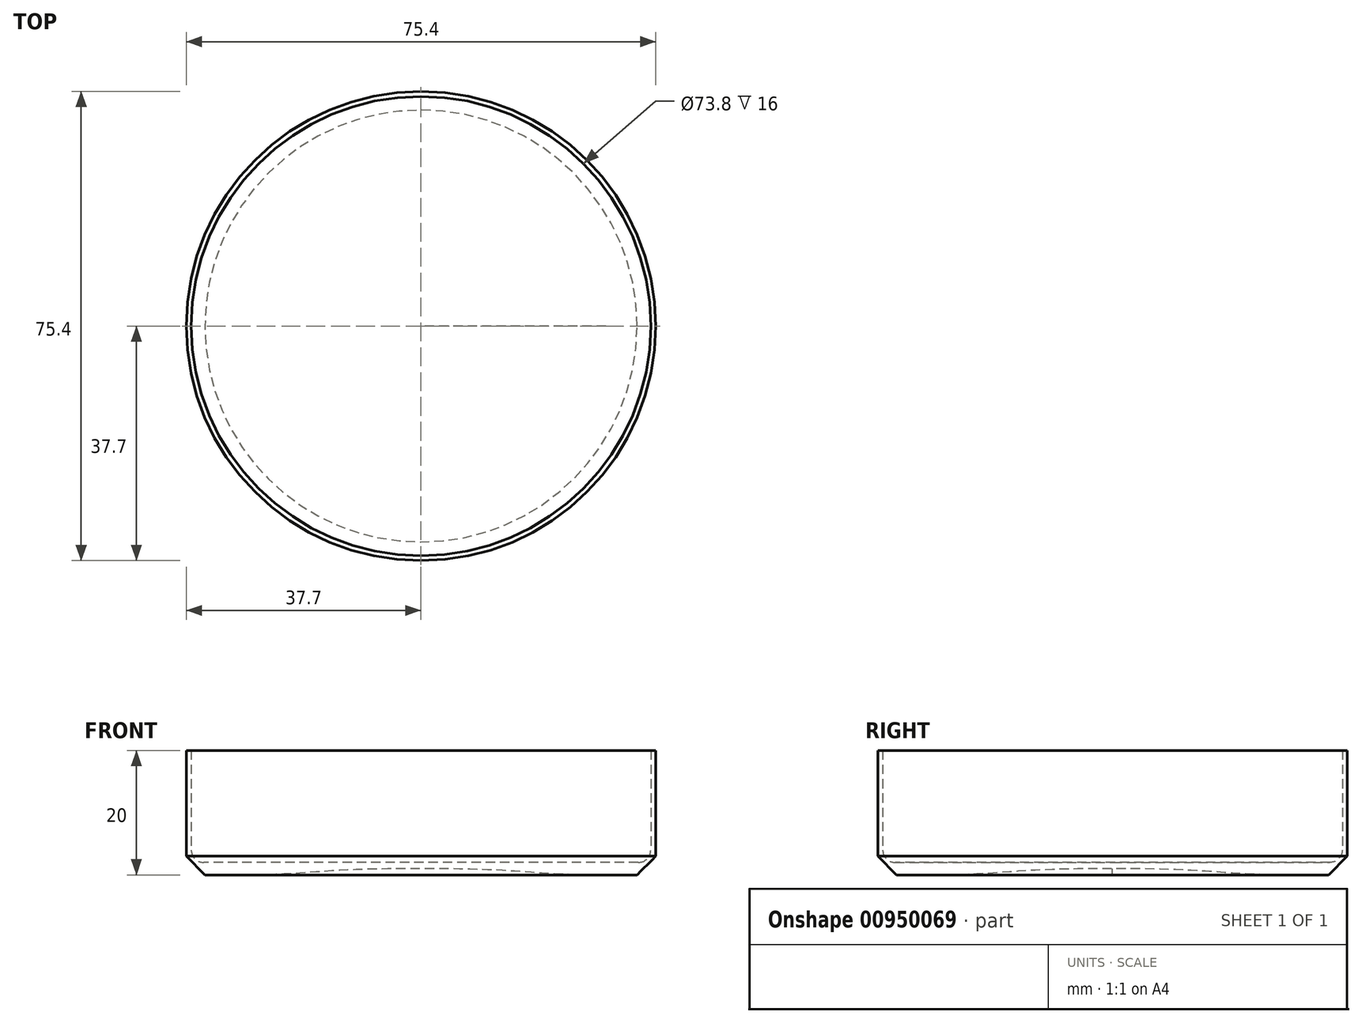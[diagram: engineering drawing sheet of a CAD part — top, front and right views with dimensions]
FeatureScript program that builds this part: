
annotation { "Feature Type Name" : "Feature", "Feature Type Description" : "" }
export const myFeature = defineFeature(function(context is Context, id is Id, definition is map)
    precondition{}
    {
        {
            var Q0;
            Q0=qCreatedBy(makeId("Front.planeOp"),FACE);
            var sketch = newSketch(context, id + "F0", { "sketchPlane" : qUnion([Q0])});
            skLineSegment(sketch, "E0", {"start": v(0, 0) * mm, "end": v(0, 38.46) * mm, "construction": true});
            skLineSegment(sketch, "E1", {"start": v(0, 0) * mm, "end": v(44.28, 0) * mm, "construction": true});
            skLineSegment(sketch, "E2", {"start": v(36.9, 0) * mm, "end": v(36.9, 38.46) * mm, "construction": true});
            skLineSegment(sketch, "E3", {"start": v(36.9, 2) * mm, "end": v(36.9, 20) * mm});
            skLineSegment(sketch, "E4", {"start": v(36.9, 20) * mm, "end": v(37.7, 20) * mm});
            skLineSegment(sketch, "E5", {"start": v(37.7, 20) * mm, "end": v(37.7, 0) * mm});
            skLineSegment(sketch, "E6", {"start": v(37.7, 0) * mm, "end": v(29.7, 0) * mm});
            skLineSegment(sketch, "E7", {"start": v(36.9, 2) * mm, "end": v(0, 2) * mm});
            skLineSegment(sketch, "E8", {"start": v(0, 2) * mm, "end": v(0, 1) * mm});
            skFitSpline(sketch, "E9", {"points": [v(29.7, 0) * mm, v(0, 1) * mm], "startDerivative": vector(-42.85, 0) * mm, "endDerivative": vector(-55, 0) * mm});
            skSolve(sketch);
        }
        {
            var Q0;
            Q0=makeQuery(id+"F0.imprint","IMPRINT",FACE,{"disambiguationData":[TD([[makeQuery(id+"F0.imprint","IMPRINT",EDGE,{"derivedFrom":sQuery(id+"F0.wireOp",EDGE,"E3")}),-1.0]])]});
            var Q1;
            Q1=sQuery(id+"F0.wireOp",EDGE,"E0");
            revolve(context, id + "F1", {"surfaceOperationType" : NewSurfaceOperationType.NEW, "entities" : qUnion([Q0]), "axis" : qUnion([Q1]), "revolveType" : RevolveType.FULL});
        }
        {
            var Q0;
            Q0=makeQuery(id+"F1.opRevolve","SWEPT_EDGE",EDGE,{"disambiguationData":[OSD([sQuery(id+"F0.wireOp",EDGE,"E3"),sQuery(id+"F0.wireOp",EDGE,"E7")])]});
            fillet(context, id + "F2", {"entities" : qUnion([Q0]), "radius" : 2 * mm, "tangentPropagation" : true, "allowEdgeOverflow" : false});
        }
        {
            var Q0;
            Q0=makeQuery(id+"F1.opRevolve","SWEPT_EDGE",EDGE,{"disambiguationData":[OSD([sQuery(id+"F0.wireOp",EDGE,"E5"),sQuery(id+"F0.wireOp",EDGE,"E6")])]});
            chamfer(context, id + "F3", {"entities" : qUnion([Q0]), "width" : 3 * mm, "tangentPropagation" : true});
        }
    });
